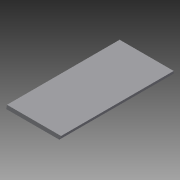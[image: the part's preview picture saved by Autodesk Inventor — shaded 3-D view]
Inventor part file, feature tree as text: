
AUTODESK INVENTOR PART (.ipt)
format: ipt  version: 2013 (Build 170138000, 138)  size: 83,456 bytes
history: native  units: mm
features: extrude x3, sketch x3
ambient origin geometry x8: Origin, YZ Plane, XZ Plane, XY Plane, X Axis, Y Axis, Z Axis, Center Point
bodies: Solid1 (feature_tree)
feature tree (6):
  extrude  "Extrusion1"  Depth=500.0mm
  extrude  "Extrusion2"  Depth=8.0mm
  extrude  "Extrusion4"  Depth=1.73189mm
  sketch  "Sketch1"  dims[d0=243.149mm d1=500.0mm]
  sketch  "Sketch2"  dims[d2=18.0mm d3=0.0mm d4=8.0mm]
  sketch  "Sketch4"  dims[d5=8.0mm d6=0.0mm d11=1.73189mm d12=10.0mm d13=0.0mm]
